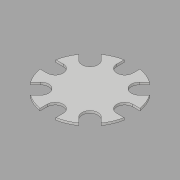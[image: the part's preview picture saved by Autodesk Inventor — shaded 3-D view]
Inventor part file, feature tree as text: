
AUTODESK INVENTOR PART (.ipt)
format: ipt  version: 2017 (Build 210142000, 142)  size: 151,040 bytes
history: native  units: in
note: dims shown in document units (in); Inventor stores cm internally (conversion verified against a paired STEP export)
features: extrude x2, sketch x2
ambient origin geometry x8: Origin, YZ Plane, XZ Plane, XY Plane, X Axis, Y Axis, Z Axis, Center Point
bodies: Solid1 (feature_tree)
feature tree (4):
  extrude  "Extrusion1"  Depth=6.0in
  extrude  "Extrusion2"  Depth=0.3937in TaperAngle=0.0deg
  sketch  "Sketch1"  dims[d0=2.75in d1=6.0in]
  sketch  "Sketch2"  dims[d2=3.1496in d4=360.0deg d6=0.3937in d7=0.0in d8=3.1496in d10=360.0deg d12=0.3937in d13=0.0in]
